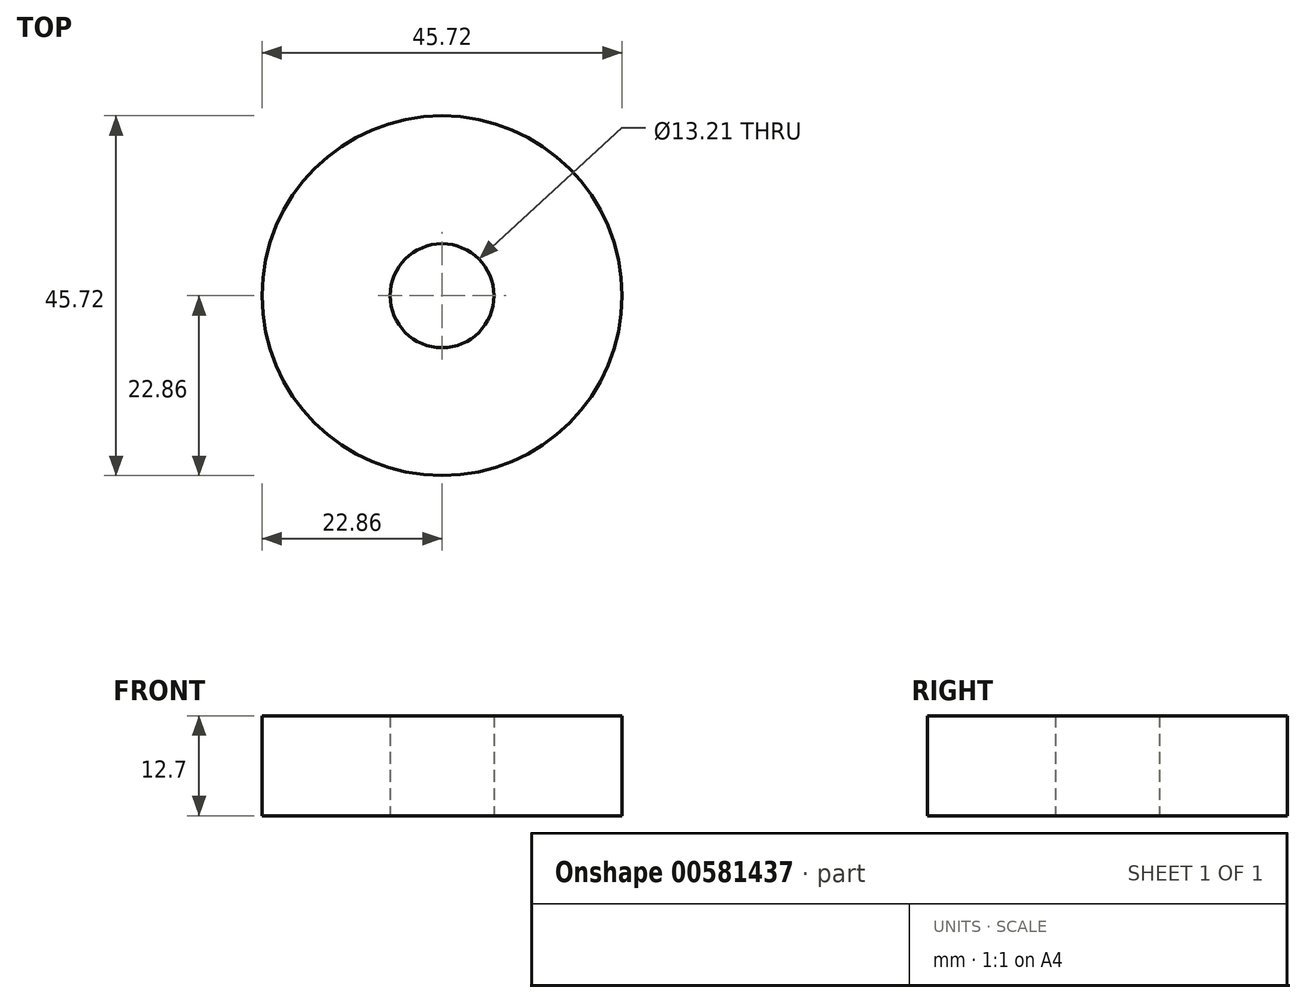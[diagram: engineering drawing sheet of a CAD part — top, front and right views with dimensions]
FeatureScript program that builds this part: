
annotation { "Feature Type Name" : "Feature", "Feature Type Description" : "" }
export const myFeature = defineFeature(function(context is Context, id is Id, definition is map)
    precondition{}
    {
        {
            var Q0;
            Q0=qCreatedBy(makeId("Top.planeOp"),FACE);
            var sketch = newSketch(context, id + "F0", { "sketchPlane" : qUnion([Q0])});
            skCircle(sketch, "E0", {"center": v(0, 0) * mm, "radius": 22.86 * mm});
            skCircle(sketch, "E1", {"center": v(0, 0) * mm, "radius": 6.6 * mm});
            skSolve(sketch);
        }
        {
            var Q0;
            Q0=makeQuery(id+"F0.imprint","IMPRINT",FACE,{"disambiguationData":[TD([[makeQuery(id+"F0.imprint","IMPRINT",EDGE,{"derivedFrom":sQuery(id+"F0.wireOp",EDGE,"E0")}),1.0]])]});
            extrude(context, id + "F1", {"entities" : qUnion([Q0]), "depth" : 12.7 * mm, "offsetDistance" : 25.4 * mm});
        }
    });
